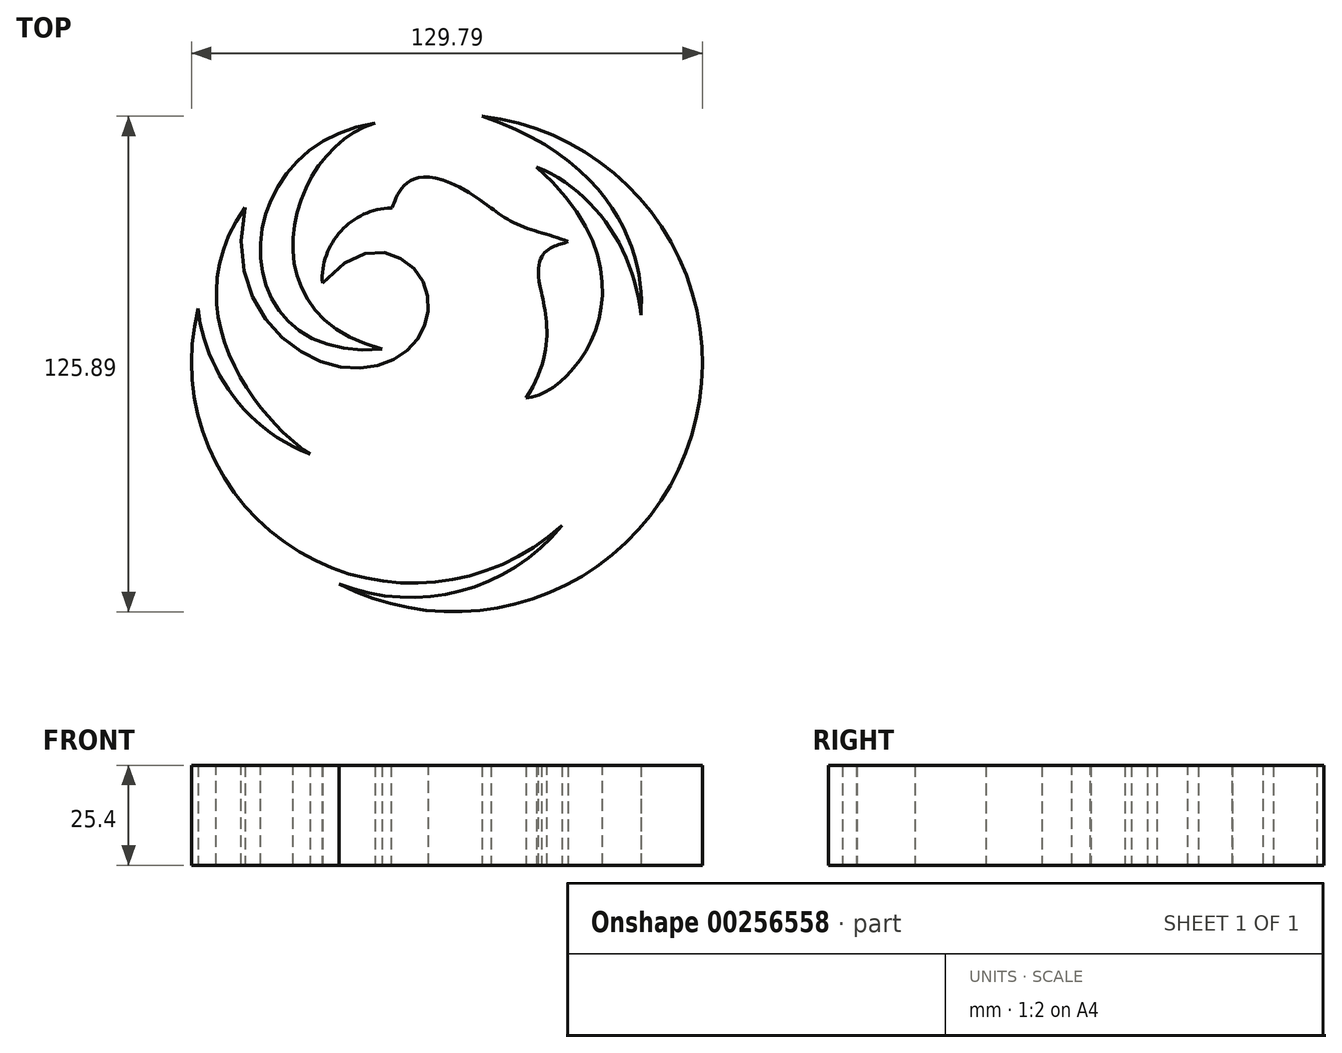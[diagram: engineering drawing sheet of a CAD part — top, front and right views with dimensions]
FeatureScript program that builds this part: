
annotation { "Feature Type Name" : "Feature", "Feature Type Description" : "" }
export const myFeature = defineFeature(function(context is Context, id is Id, definition is map)
    precondition{}
    {
        {
            var Q0;
            Q0=qCreatedBy(makeId("Top.planeOp"),FACE);
            var sketch = newSketch(context, id + "F0", { "sketchPlane" : qUnion([Q0])});
            skPoint(sketch, "E0", {"position": v(0, 64.74) * mm});
            skPoint(sketch, "E1", {"position": v(0, -64.74) * mm});
            skLineSegment(sketch, "E2", {"start": v(0, 64.74) * mm, "end": v(0, -64.74) * mm, "construction": true});
            skPoint(sketch, "E3", {"position": v(0, 0) * mm});
            skArc(sketch, "E4", {"start": v(-27.38, -55.57) * mm, "mid": v(62.12, -18) * mm, "end": v(8.97, 63.2) * mm});
            skArc(sketch, "E5", {"start": v(-27.38, -55.57) * mm, "mid": v(3.36, -57.45) * mm, "end": v(29.23, -40.73) * mm});
            skArc(sketch, "E6", {"start": v(-63.25, 14.33) * mm, "mid": v(-37.44, -47.5) * mm, "end": v(29.23, -40.73) * mm});
            skArc(sketch, "E7", {"start": v(-14.16, 39.94) * mm, "mid": v(-26.95, 34.09) * mm, "end": v(-31.67, 20.83) * mm});
            skFitSpline(sketch, "E8", {"points": [v(-14.16, 39.94) * mm, v(11.16, 39.94) * mm], "startDerivative": vector(3.52, -0.95) * mm, "endDerivative": vector(69.63, -53.65) * mm});
            skFitSpline(sketch, "E9", {"points": [v(11.16, 39.94) * mm, v(19.38, 35.11) * mm, v(30.78, 31.34) * mm], "startDerivative": vector(13.85, -11.33) * mm, "endDerivative": vector(20.98, -9.04) * mm});
            skFitSpline(sketch, "E10", {"points": [v(30.78, 31.34) * mm, v(23.98, 18.43) * mm], "startDerivative": vector(-9.63, -3.58) * mm, "endDerivative": vector(9, -35.03) * mm});
            skFitSpline(sketch, "E11", {"points": [v(23.98, 18.43) * mm, v(20.08, -8.4) * mm], "startDerivative": vector(4, -18.36) * mm, "endDerivative": vector(-22.4, -33.86) * mm});
            skFitSpline(sketch, "E12", {"points": [v(20.08, -8.4) * mm, v(22.78, 50.36) * mm], "startDerivative": vector(34.85, 1.92) * mm, "endDerivative": vector(-99.1, 88.07) * mm});
            skFitSpline(sketch, "E13", {"points": [v(22.78, 50.36) * mm, v(49.24, 12.66) * mm], "startDerivative": vector(43.65, -17.95) * mm, "endDerivative": vector(4.73, -50.41) * mm});
            skFitSpline(sketch, "E14", {"points": [v(49.24, 12.66) * mm, v(8.97, 63.2) * mm], "startDerivative": vector(3.31, 41.42) * mm, "endDerivative": vector(-105.91, 35.44) * mm});
            skFitSpline(sketch, "E15", {"points": [v(-18.33, 61.43) * mm, v(-16.43, 4.08) * mm], "startDerivative": vector(-64.07, -17.4) * mm, "endDerivative": vector(108.6, -27) * mm});
            skFitSpline(sketch, "E16", {"points": [v(-16.43, 4.08) * mm, v(-18.33, 61.43) * mm], "startDerivative": vector(-124.64, -12.23) * mm, "endDerivative": vector(115.57, 17.26) * mm});
            skFitSpline(sketch, "E17", {"points": [v(-63.25, 14.33) * mm, v(-34.82, -22.6) * mm], "startDerivative": vector(4.6, -43) * mm, "endDerivative": vector(51.6, -19.4) * mm});
            skFitSpline(sketch, "E18", {"points": [v(-34.82, -22.6) * mm, v(-51.3, 39.96) * mm], "startDerivative": vector(-34.56, 22.25) * mm, "endDerivative": vector(58.46, 81.9) * mm});
            skFitSpline(sketch, "E19", {"points": [v(-51.3, 39.96) * mm, v(-29.08, 0) * mm, v(-7.76, 6.21) * mm, v(-6.94, 22.6) * mm, v(-31.67, 20.83) * mm], "startDerivative": vector(-43.8, -205.13) * mm, "endDerivative": vector(-130.76, -150.58) * mm});
            skSolve(sketch);
        }
        {
            var Q0;
            Q0 = qSketchRegion(id + "F0", true);
            extrude(context, id + "F1", {"entities" : qUnion([Q0]), "depth" : 25.4 * mm, "offsetDistance" : 25.4 * mm});
        }
        {
            var Q0;
            Q0 = qSketchRegion(id + "F0", true);
            extrude(context, id + "F2", {"entities" : qUnion([Q0]), "depth" : 25.4 * mm, "offsetDistance" : 25.4 * mm});
        }
    });
